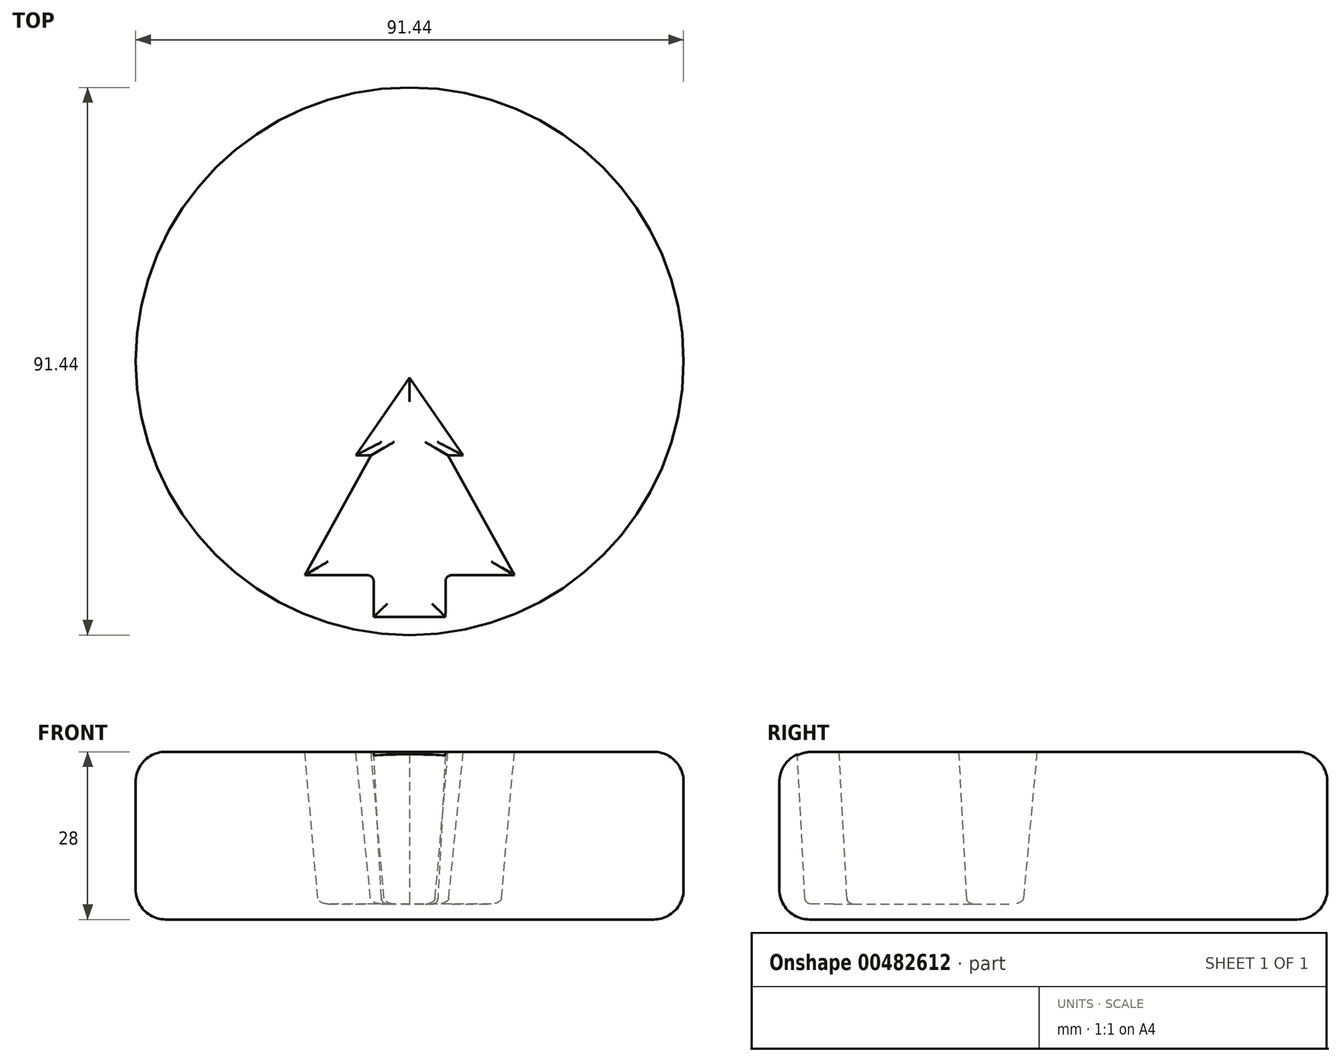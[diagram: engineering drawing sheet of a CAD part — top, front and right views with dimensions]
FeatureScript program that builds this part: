
annotation { "Feature Type Name" : "Feature", "Feature Type Description" : "" }
export const myFeature = defineFeature(function(context is Context, id is Id, definition is map)
    precondition{}
    {
        {
            var Q0;
            Q0=qCreatedBy(makeId("Top.planeOp"),FACE);
            var sketch = newSketch(context, id + "F0", { "sketchPlane" : qUnion([Q0])});
            skCircle(sketch, "E0", {"center": v(0, 0) * mm, "radius": 45.72 * mm});
            skSolve(sketch);
        }
        {
            var Q0;
            Q0=qSketchRegion(id+"F0",true);
            extrude(context, id + "F1", {"entities" : qUnion([Q0]), "depth" : 28 * mm});
        }
        {
            var Q0;
            Q0=makeQuery(id+"F1.opExtrude","CAP_FACE",FACE,{"disambiguationData":[OSD([sQuery(id+"F0.wireOp",EDGE,"E0")])],"isStart":false});
            var sketch = newSketch(context, id + "F2", { "sketchPlane" : qUnion([Q0])});
            skLineSegment(sketch, "E1", {"start": v(6, -42.73) * mm, "end": v(-6, -42.73) * mm});
            skLineSegment(sketch, "E2", {"start": v(-6, -42.73) * mm, "end": v(-6, -36.73) * mm});
            skLineSegment(sketch, "E3", {"start": v(-7, -35.73) * mm, "end": v(-17.5, -35.73) * mm});
            skLineSegment(sketch, "E4", {"start": v(-17.5, -35.73) * mm, "end": v(-6.43, -15.73) * mm});
            skLineSegment(sketch, "E5", {"start": v(-6.43, -15.73) * mm, "end": v(-8.97, -15.73) * mm});
            skLineSegment(sketch, "E6", {"start": v(-8.97, -15.73) * mm, "end": v(0, -2.73) * mm});
            skLineSegment(sketch, "E7.MirrorCS", {"start": v(8.97, -15.73) * mm, "end": v(0, -2.73) * mm});
            skLineSegment(sketch, "E8.MirrorCS", {"start": v(6, -42.73) * mm, "end": v(6, -36.73) * mm});
            skLineSegment(sketch, "E9.MirrorCS", {"start": v(6.43, -15.73) * mm, "end": v(8.97, -15.73) * mm});
            skLineSegment(sketch, "E10.MirrorCS", {"start": v(7, -35.73) * mm, "end": v(17.5, -35.73) * mm});
            skLineSegment(sketch, "E11.MirrorCS", {"start": v(17.5, -35.73) * mm, "end": v(6.43, -15.73) * mm});
            skLineSegment(sketch, "E12", {"start": v(0, -42.73) * mm, "end": v(0, -2.73) * mm, "construction": true});
            skPoint(sketch, "E13.visualSharp", {"position": v(-6, -35.73) * mm});
            skArc(sketch, "E13.filletArc", {"start": v(-6, -36.73) * mm, "mid": v(-6.3, -36.03) * mm, "end": v(-7, -35.73) * mm});
            skPoint(sketch, "E14.visualSharp", {"position": v(6, -35.73) * mm});
            skArc(sketch, "E14.filletArc", {"start": v(7, -35.73) * mm, "mid": v(6.3, -36.03) * mm, "end": v(6, -36.73) * mm});
            skLineSegment(sketch, "E15", {"start": v(0, 0) * mm, "end": v(0, -45.72) * mm, "construction": true});
            skSolve(sketch);
        }
        {
            var Q0;
            Q0=makeQuery(id+"F2.imprint","IMPRINT",FACE,{"disambiguationData":[TD([[makeQuery(id+"F2.imprint","IMPRINT",EDGE,{"derivedFrom":sQuery(id+"F2.wireOp",EDGE,"E1")}),-1.0]])]});
            extrude(context, id + "F3", {"entities" : qUnion([Q0]), "operationType" : NewBodyOperationType.REMOVE, "oppositeDirection" : true, "depth" : 25.4 * mm, "hasDraft" : true, "draftAngle" : 3 * degree, "draftPullDirection" : true});
        }
        {
            var Q0;
            Q0=makeQuery(id+"F1.opExtrude","CAP_EDGE",EDGE,{"disambiguationData":[OSD([sQuery(id+"F0.wireOp",EDGE,"E0")])],"isStart":false});
            var Q1;
            Q1=makeQuery(id+"F1.opExtrude","CAP_EDGE",EDGE,{"disambiguationData":[OSD([sQuery(id+"F0.wireOp",EDGE,"E0")])],"isStart":true});
            fillet(context, id + "F4", {"entities" : qUnion([Q0, Q1]), "radius" : 5 * mm, "tangentPropagation" : true, "allowEdgeOverflow" : false});
        }
        {
            var Q0;
            Q0=makeQuery(id+"Fkw29PR0jKbgysm_1.4.F3.boolean.opBoolean","COPY",FACE,{"derivedFrom":makeQuery(id+"Fkw29PR0jKbgysm_1.4.F3.opExtrude","CAP_FACE",FACE,{"disambiguationData":[OSD([sQuery(id+"F2.wireOp",EDGE,"E1"),sQuery(id+"F2.wireOp",EDGE,"E2"),sQuery(id+"F2.wireOp",EDGE,"E3"),sQuery(id+"F2.wireOp",EDGE,"E4"),sQuery(id+"F2.wireOp",EDGE,"E5"),sQuery(id+"F2.wireOp",EDGE,"E6"),sQuery(id+"F2.wireOp",EDGE,"E7.MirrorCS"),sQuery(id+"F2.wireOp",EDGE,"E8.MirrorCS"),sQuery(id+"F2.wireOp",EDGE,"E9.MirrorCS"),sQuery(id+"F2.wireOp",EDGE,"E10.MirrorCS"),sQuery(id+"F2.wireOp",EDGE,"E11.MirrorCS"),sQuery(id+"F2.wireOp",EDGE,"E13.filletArc"),sQuery(id+"F2.wireOp",EDGE,"E14.filletArc")])],"isStart":false})});
            var Q1;
            Q1=makeQuery(id+"Fkw29PR0jKbgysm_1.5.F3.boolean.opBoolean","COPY",FACE,{"derivedFrom":makeQuery(id+"Fkw29PR0jKbgysm_1.5.F3.opExtrude","CAP_FACE",FACE,{"disambiguationData":[OSD([sQuery(id+"F2.wireOp",EDGE,"E1"),sQuery(id+"F2.wireOp",EDGE,"E2"),sQuery(id+"F2.wireOp",EDGE,"E3"),sQuery(id+"F2.wireOp",EDGE,"E4"),sQuery(id+"F2.wireOp",EDGE,"E5"),sQuery(id+"F2.wireOp",EDGE,"E6"),sQuery(id+"F2.wireOp",EDGE,"E7.MirrorCS"),sQuery(id+"F2.wireOp",EDGE,"E8.MirrorCS"),sQuery(id+"F2.wireOp",EDGE,"E9.MirrorCS"),sQuery(id+"F2.wireOp",EDGE,"E10.MirrorCS"),sQuery(id+"F2.wireOp",EDGE,"E11.MirrorCS"),sQuery(id+"F2.wireOp",EDGE,"E13.filletArc"),sQuery(id+"F2.wireOp",EDGE,"E14.filletArc")])],"isStart":false})});
            var Q2;
            Q2=makeQuery(id+"F3.boolean.opBoolean","COPY",FACE,{"derivedFrom":makeQuery(id+"F3.opExtrude","CAP_FACE",FACE,{"disambiguationData":[OSD([sQuery(id+"F2.wireOp",EDGE,"E1"),sQuery(id+"F2.wireOp",EDGE,"E2"),sQuery(id+"F2.wireOp",EDGE,"E3"),sQuery(id+"F2.wireOp",EDGE,"E4"),sQuery(id+"F2.wireOp",EDGE,"E5"),sQuery(id+"F2.wireOp",EDGE,"E6"),sQuery(id+"F2.wireOp",EDGE,"E7.MirrorCS"),sQuery(id+"F2.wireOp",EDGE,"E8.MirrorCS"),sQuery(id+"F2.wireOp",EDGE,"E9.MirrorCS"),sQuery(id+"F2.wireOp",EDGE,"E10.MirrorCS"),sQuery(id+"F2.wireOp",EDGE,"E11.MirrorCS"),sQuery(id+"F2.wireOp",EDGE,"E13.filletArc"),sQuery(id+"F2.wireOp",EDGE,"E14.filletArc")])],"isStart":false})});
            var Q3;
            Q3=makeQuery(id+"Fkw29PR0jKbgysm_1.1.F3.boolean.opBoolean","COPY",FACE,{"derivedFrom":makeQuery(id+"Fkw29PR0jKbgysm_1.1.F3.opExtrude","CAP_FACE",FACE,{"disambiguationData":[OSD([sQuery(id+"F2.wireOp",EDGE,"E1"),sQuery(id+"F2.wireOp",EDGE,"E2"),sQuery(id+"F2.wireOp",EDGE,"E3"),sQuery(id+"F2.wireOp",EDGE,"E4"),sQuery(id+"F2.wireOp",EDGE,"E5"),sQuery(id+"F2.wireOp",EDGE,"E6"),sQuery(id+"F2.wireOp",EDGE,"E7.MirrorCS"),sQuery(id+"F2.wireOp",EDGE,"E8.MirrorCS"),sQuery(id+"F2.wireOp",EDGE,"E9.MirrorCS"),sQuery(id+"F2.wireOp",EDGE,"E10.MirrorCS"),sQuery(id+"F2.wireOp",EDGE,"E11.MirrorCS"),sQuery(id+"F2.wireOp",EDGE,"E13.filletArc"),sQuery(id+"F2.wireOp",EDGE,"E14.filletArc")])],"isStart":false})});
            var Q4;
            Q4=makeQuery(id+"Fkw29PR0jKbgysm_1.2.F3.boolean.opBoolean","COPY",FACE,{"derivedFrom":makeQuery(id+"Fkw29PR0jKbgysm_1.2.F3.opExtrude","CAP_FACE",FACE,{"disambiguationData":[OSD([sQuery(id+"F2.wireOp",EDGE,"E1"),sQuery(id+"F2.wireOp",EDGE,"E2"),sQuery(id+"F2.wireOp",EDGE,"E3"),sQuery(id+"F2.wireOp",EDGE,"E4"),sQuery(id+"F2.wireOp",EDGE,"E5"),sQuery(id+"F2.wireOp",EDGE,"E6"),sQuery(id+"F2.wireOp",EDGE,"E7.MirrorCS"),sQuery(id+"F2.wireOp",EDGE,"E8.MirrorCS"),sQuery(id+"F2.wireOp",EDGE,"E9.MirrorCS"),sQuery(id+"F2.wireOp",EDGE,"E10.MirrorCS"),sQuery(id+"F2.wireOp",EDGE,"E11.MirrorCS"),sQuery(id+"F2.wireOp",EDGE,"E13.filletArc"),sQuery(id+"F2.wireOp",EDGE,"E14.filletArc")])],"isStart":false})});
            var Q5;
            Q5=makeQuery(id+"Fkw29PR0jKbgysm_1.3.F3.boolean.opBoolean","COPY",FACE,{"derivedFrom":makeQuery(id+"Fkw29PR0jKbgysm_1.3.F3.opExtrude","CAP_FACE",FACE,{"disambiguationData":[OSD([sQuery(id+"F2.wireOp",EDGE,"E1"),sQuery(id+"F2.wireOp",EDGE,"E2"),sQuery(id+"F2.wireOp",EDGE,"E3"),sQuery(id+"F2.wireOp",EDGE,"E4"),sQuery(id+"F2.wireOp",EDGE,"E5"),sQuery(id+"F2.wireOp",EDGE,"E6"),sQuery(id+"F2.wireOp",EDGE,"E7.MirrorCS"),sQuery(id+"F2.wireOp",EDGE,"E8.MirrorCS"),sQuery(id+"F2.wireOp",EDGE,"E9.MirrorCS"),sQuery(id+"F2.wireOp",EDGE,"E10.MirrorCS"),sQuery(id+"F2.wireOp",EDGE,"E11.MirrorCS"),sQuery(id+"F2.wireOp",EDGE,"E13.filletArc"),sQuery(id+"F2.wireOp",EDGE,"E14.filletArc")])],"isStart":false})});
            fillet(context, id + "F5", {"entities" : qUnion([Q0, Q1, Q2, Q3, Q4, Q5]), "radius" : 1 * mm, "tangentPropagation" : true, "allowEdgeOverflow" : false});
        }
    });
